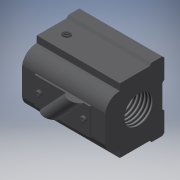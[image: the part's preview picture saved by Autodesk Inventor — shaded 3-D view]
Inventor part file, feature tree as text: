
AUTODESK INVENTOR PART (.ipt)
format: ipt  version: 2016 (Build 200138000, 138)  size: 229,376 bytes
history: native  units: mm
features: sketch x9, other x7, extrude x5, revolve x2, hole x2, pattern_linear x1, thread x1
ambient origin geometry x8: Origin, YZ Plane, XZ Plane, XY Plane, X Axis, Y Axis, Z Axis, Center Point
bodies: Solid1 (feature_tree)
feature tree (27):
  extrude  "Extrusion1"  Depth=58.0mm TaperAngle=0.0deg
  extrude  "Extrusion2"  TaperAngle=360.0deg  [1 undecoded]
  extrude  "Extrusion3"  Depth=0.8mm TaperAngle=0.0deg
  revolve  "Revolution1"  [1 undecoded]
  revolve  "Revolution2"  [1 undecoded]
  extrude  "Extrusion4"  [1 undecoded]
  extrude  "Extrusion5"  [1 undecoded]
  hole  "Hole1"  [1 undecoded]
  hole  "Hole2"  [1 undecoded]
  pattern_linear  "Rectangular Pattern1"  [2 undecoded]
  other  "bnt_nut_1_XY"
  other  "bnt_nut_1_YZ"
  other  "bnt_nut_1_ZX"
  other  "bnt_nut_1_X"
  other  "bnt_nut_1_Y"
  other  "bnt_nut_1_Z"
  other  "bnt_nut_1_Center"
  thread  "Thread1"  [1 undecoded]
  sketch  "Sketch_1"  dims[d0=58.0mm d1=0.0mm d2=58.0mm d3=0.0mm]
  sketch  "Sketch_2"  dims[d4=4.6mm d5=0.0mm d6=360.0deg]
  sketch  "Sketch_3"  dims[d7=360.0deg d8=0.8mm d9=0.0mm]
  sketch  "Sketch_4"  dims[d10=0.8mm d11=0.0mm]
  sketch  "Sketch_5"  dims[d12=4.917mm d13=10.5415mm d14=6.0mm d15=2.0mm d16=90.0deg d17=14.140584mm d18=120.0deg]
  sketch  "Sketch_6"  dims[d19=4.917mm d20=10.5415mm d21=6.0mm d22=2.0mm d23=90.0deg d24=13.140584mm d25=120.0deg d26=20.0mm d28=35.0mm d29=20.0mm d31=35.0mm]
  sketch  "Sketch_7"  dims[d32=0.0mm d33=10.0mm d34=0.0mm]
  sketch  "Sketch8"
  sketch  "Sketch9"
note: 10 required parameter values undecoded (feature->parameter linkage not recoverable at this tier; creation-order binding heuristic only, values carry confidence <= 0.55)